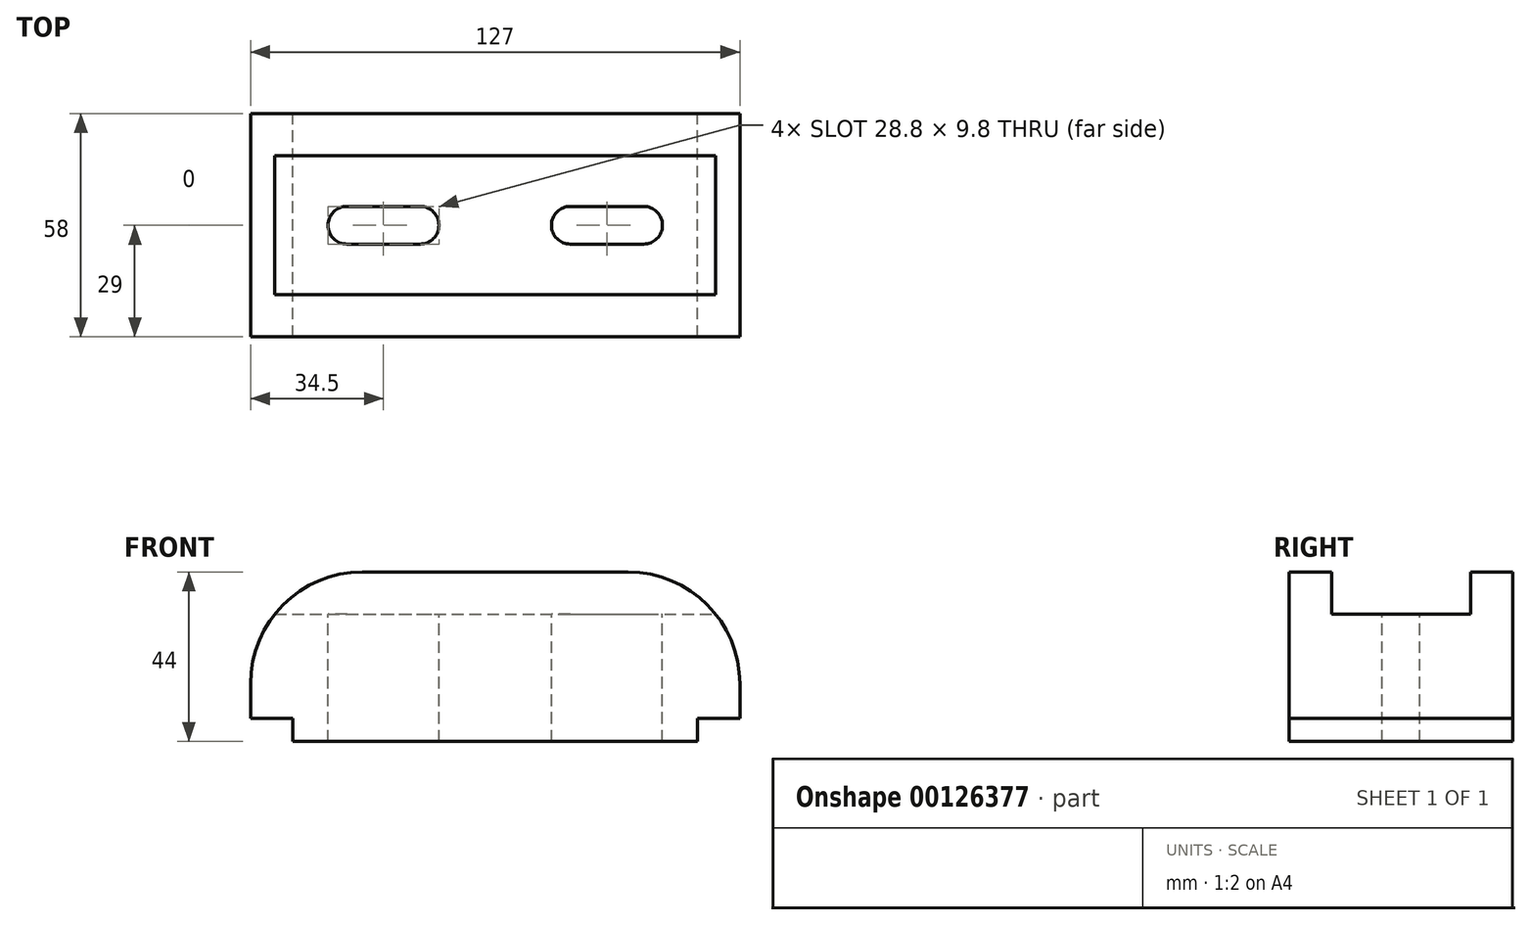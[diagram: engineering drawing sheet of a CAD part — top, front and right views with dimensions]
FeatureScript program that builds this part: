
annotation { "Feature Type Name" : "Feature", "Feature Type Description" : "" }
export const myFeature = defineFeature(function(context is Context, id is Id, definition is map)
    precondition{}
    {
        {
            var Q0;
            Q0=qCreatedBy(makeId("Front.planeOp"),FACE);
            var sketch = newSketch(context, id + "F0", { "sketchPlane" : qUnion([Q0])});
            skLineSegment(sketch, "E0", {"start": v(11, 0) * mm, "end": v(116, 0) * mm});
            skLineSegment(sketch, "E1", {"start": v(116, 0) * mm, "end": v(116, 6) * mm});
            skLineSegment(sketch, "E2", {"start": v(116, 6) * mm, "end": v(127, 6) * mm});
            skLineSegment(sketch, "E3", {"start": v(11, 0) * mm, "end": v(11, 6) * mm});
            skLineSegment(sketch, "E4", {"start": v(11, 6) * mm, "end": v(0, 6) * mm});
            skLineSegment(sketch, "E5", {"start": v(0, 6) * mm, "end": v(0, 44) * mm});
            skLineSegment(sketch, "E6", {"start": v(0, 44) * mm, "end": v(127, 44) * mm});
            skLineSegment(sketch, "E7", {"start": v(127, 44) * mm, "end": v(127, 6) * mm});
            skSolve(sketch);
        }
        {
            var Q0;
            Q0 = qSketchRegion(id + "F0", true);
            extrude(context, id + "F1", {"entities" : qUnion([Q0]), "endBound" : BoundingType.SYMMETRIC, "depth" : 58 * mm});
        }
        {
            var Q0;
            Q0=makeQuery(id+"F1.opExtrude","SWEPT_FACE",FACE,{"disambiguationData":[OSD([sQuery(id+"F0.wireOp",EDGE,"E7")])]});
            var sketch = newSketch(context, id + "F2", { "sketchPlane" : qUnion([Q0])});
            skLineSegment(sketch, "E8.bottom", {"start": v(-18, 44) * mm, "end": v(18, 44) * mm});
            skLineSegment(sketch, "E8.top", {"start": v(-18, 33) * mm, "end": v(18, 33) * mm});
            skLineSegment(sketch, "E8.left", {"start": v(-18, 44) * mm, "end": v(-18, 33) * mm});
            skLineSegment(sketch, "E8.right", {"start": v(18, 44) * mm, "end": v(18, 33) * mm});
            skSolve(sketch);
        }
        {
            var Q0;
            Q0 = qSketchRegion(id + "F2", true);
            extrude(context, id + "F3", {"entities" : qUnion([Q0]), "operationType" : NewBodyOperationType.REMOVE, "endBound" : BoundingType.THROUGH_ALL, "oppositeDirection" : true, "depth" : 127 * mm});
        }
        {
            var Q0;
            Q0=makeQuery(id+"F1.opExtrude","CAP_FACE",FACE,{"disambiguationData":[OSD([sQuery(id+"F0.wireOp",EDGE,"E0"),sQuery(id+"F0.wireOp",EDGE,"E1"),sQuery(id+"F0.wireOp",EDGE,"E2"),sQuery(id+"F0.wireOp",EDGE,"E3"),sQuery(id+"F0.wireOp",EDGE,"E4"),sQuery(id+"F0.wireOp",EDGE,"E5"),sQuery(id+"F0.wireOp",EDGE,"E6"),sQuery(id+"F0.wireOp",EDGE,"E7")])],"isStart":false});
            var sketch = newSketch(context, id + "F4", { "sketchPlane" : qUnion([Q0])});
            skArc(sketch, "E9", {"start": v(29, 44) * mm, "mid": v(8.5, 35.5) * mm, "end": v(0, 15) * mm});
            skLineSegment(sketch, "E10", {"start": v(0, 15) * mm, "end": v(0, 44) * mm});
            skLineSegment(sketch, "E11", {"start": v(0, 44) * mm, "end": v(29, 44) * mm});
            skSolve(sketch);
        }
        {
            var Q0;
            Q0 = qSketchRegion(id + "F4", true);
            extrude(context, id + "F5", {"entities" : qUnion([Q0]), "operationType" : NewBodyOperationType.REMOVE, "endBound" : BoundingType.THROUGH_ALL, "oppositeDirection" : true, "depth" : 25 * mm});
        }
        {
            var Q0;
            Q0=makeQuery(id+"F1.opExtrude","CAP_FACE",FACE,{"disambiguationData":[OSD([sQuery(id+"F0.wireOp",EDGE,"E0"),sQuery(id+"F0.wireOp",EDGE,"E1"),sQuery(id+"F0.wireOp",EDGE,"E2"),sQuery(id+"F0.wireOp",EDGE,"E3"),sQuery(id+"F0.wireOp",EDGE,"E4"),sQuery(id+"F0.wireOp",EDGE,"E5"),sQuery(id+"F0.wireOp",EDGE,"E6"),sQuery(id+"F0.wireOp",EDGE,"E7")])],"isStart":false});
            var sketch = newSketch(context, id + "F6", { "sketchPlane" : qUnion([Q0])});
            skArc(sketch, "E12", {"start": v(127, 15) * mm, "mid": v(118.5, 35.5) * mm, "end": v(98, 44) * mm});
            skLineSegment(sketch, "E13", {"start": v(98, 44) * mm, "end": v(127, 44) * mm});
            skLineSegment(sketch, "E14", {"start": v(127, 44) * mm, "end": v(127, 15) * mm});
            skSolve(sketch);
        }
        {
            var Q0;
            Q0 = qSketchRegion(id + "F6", true);
            extrude(context, id + "F7", {"entities" : qUnion([Q0]), "operationType" : NewBodyOperationType.REMOVE, "endBound" : BoundingType.THROUGH_ALL, "oppositeDirection" : true, "depth" : 25 * mm});
        }
        {
            var Q0;
            Q0=makeQuery(id+"F3.boolean.opBoolean","COPY",FACE,{"derivedFrom":makeQuery(id+"F3.opExtrude","SWEPT_FACE",FACE,{"disambiguationData":[OSD([sQuery(id+"F2.wireOp",EDGE,"E8.top")])]})});
            var sketch = newSketch(context, id + "F8", { "sketchPlane" : qUnion([Q0])});
            skLineSegment(sketch, "E15", {"start": v(25, 4.9) * mm, "end": v(44, 4.9) * mm});
            skLineSegment(sketch, "E16", {"start": v(25, -4.9) * mm, "end": v(44, -4.9) * mm});
            skLineSegment(sketch, "E17", {"start": v(83, 4.9) * mm, "end": v(102, 4.9) * mm});
            skLineSegment(sketch, "E18", {"start": v(83, -4.9) * mm, "end": v(102, -4.9) * mm});
            skArc(sketch, "E19", {"start": v(25, 4.9) * mm, "mid": v(20.1, 0) * mm, "end": v(25, -4.9) * mm});
            skArc(sketch, "E20", {"start": v(44, -4.9) * mm, "mid": v(48.9, 0) * mm, "end": v(44, 4.9) * mm});
            skArc(sketch, "E21", {"start": v(83, 4.9) * mm, "mid": v(78.1, 0) * mm, "end": v(83, -4.9) * mm});
            skArc(sketch, "E22", {"start": v(102, -4.9) * mm, "mid": v(106.9, 0) * mm, "end": v(102, 4.9) * mm});
            skSolve(sketch);
        }
        {
            var Q0;
            Q0=makeQuery(id+"F8.imprint","IMPRINT",FACE,{"disambiguationData":[TD([[makeQuery(id+"F8.imprint","IMPRINT",EDGE,{"derivedFrom":sQuery(id+"F8.wireOp",EDGE,"E17")}),-1.0]])]});
            var Q1;
            Q1=makeQuery(id+"F8.imprint","IMPRINT",FACE,{"disambiguationData":[TD([[makeQuery(id+"F8.imprint","IMPRINT",EDGE,{"derivedFrom":sQuery(id+"F8.wireOp",EDGE,"E15")}),-1.0]])]});
            extrude(context, id + "F9", {"entities" : qUnion([Q0, Q1]), "operationType" : NewBodyOperationType.REMOVE, "endBound" : BoundingType.THROUGH_ALL, "oppositeDirection" : true, "depth" : 25 * mm});
        }
    });
